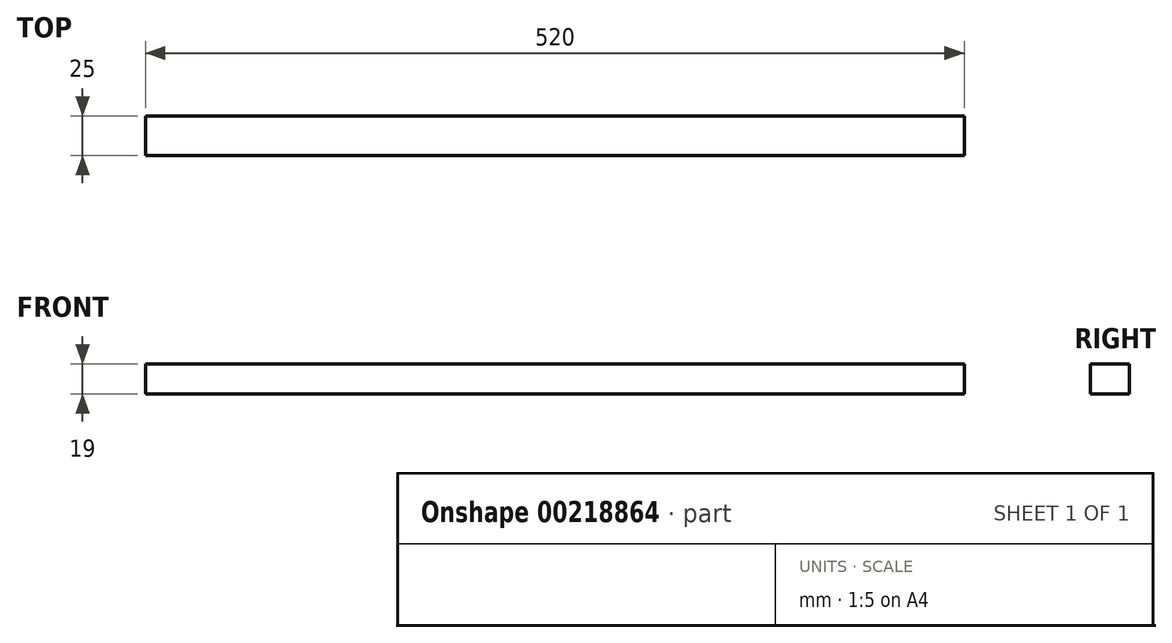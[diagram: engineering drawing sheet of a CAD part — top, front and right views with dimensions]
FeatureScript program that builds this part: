
annotation { "Feature Type Name" : "Feature", "Feature Type Description" : "" }
export const myFeature = defineFeature(function(context is Context, id is Id, definition is map)
    precondition{}
    {
        {
            var Q0;
            Q0=qCreatedBy(makeId("Front.planeOp"),FACE);
            var sketch = newSketch(context, id + "F0", { "sketchPlane" : qUnion([Q0])});
            skLineSegment(sketch, "E0.bottom", {"start": v(-260.55, -10.48) * mm, "end": v(259.45, -10.48) * mm});
            skLineSegment(sketch, "E0.top", {"start": v(-260.55, -29.48) * mm, "end": v(259.45, -29.48) * mm});
            skLineSegment(sketch, "E0.left", {"start": v(-260.55, -10.48) * mm, "end": v(-260.55, -29.48) * mm});
            skLineSegment(sketch, "E0.right", {"start": v(259.45, -10.48) * mm, "end": v(259.45, -29.48) * mm});
            skSolve(sketch);
        }
        {
            var Q0;
            Q0 = qSketchRegion(id + "F0", true);
            extrude(context, id + "F1", {"entities" : qUnion([Q0]), "depth" : 25 * mm});
        }
    });
